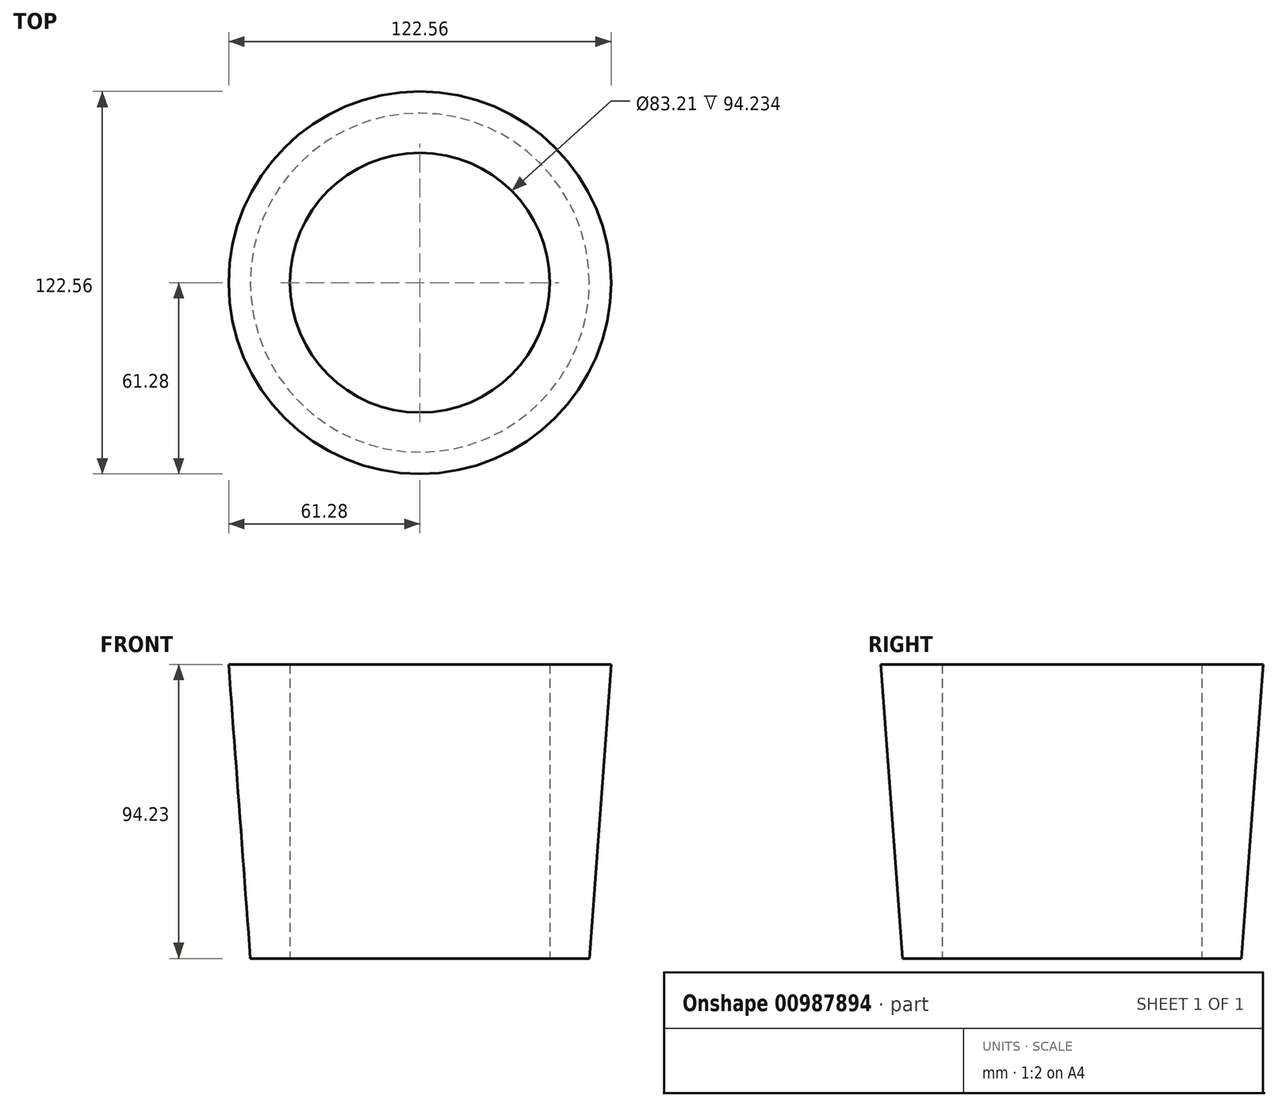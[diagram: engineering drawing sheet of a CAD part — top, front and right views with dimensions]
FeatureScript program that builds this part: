
annotation { "Feature Type Name" : "Feature", "Feature Type Description" : "" }
export const myFeature = defineFeature(function(context is Context, id is Id, definition is map)
    precondition{}
    {
        {
            var Q0;
            Q0=qCreatedBy(makeId("Front.planeOp"),FACE);
            var sketch = newSketch(context, id + "F0", { "sketchPlane" : qUnion([Q0])});
            skLineSegment(sketch, "E0", {"start": v(0, 0) * mm, "end": v(0, 44.65) * mm, "construction": true});
            skLineSegment(sketch, "E1", {"start": v(-61.28, 51.18) * mm, "end": v(-54.3, -43.05) * mm});
            skLineSegment(sketch, "E2", {"start": v(-54.3, -43.05) * mm, "end": v(-41.6, -43.05) * mm});
            skLineSegment(sketch, "E3", {"start": v(-54.3, -43.05) * mm, "end": v(0, -43.05) * mm, "construction": true});
            skLineSegment(sketch, "E4", {"start": v(-41.6, -43.05) * mm, "end": v(-41.6, 51.18) * mm});
            skLineSegment(sketch, "E5", {"start": v(-61.28, 51.18) * mm, "end": v(-41.6, 51.18) * mm});
            skLineSegment(sketch, "E6", {"start": v(-41.6, 51.18) * mm, "end": v(-36.53, 51.18) * mm});
            skLineSegment(sketch, "E7", {"start": v(-41.6, -43.05) * mm, "end": v(-36.53, 51.18) * mm});
            skSolve(sketch);
        }
        {
            var Q0;
            Q0=makeQuery(id+"F0.imprint","IMPRINT",FACE,{"disambiguationData":[TD([[makeQuery(id+"F0.imprint","IMPRINT",EDGE,{"derivedFrom":sQuery(id+"F0.wireOp",EDGE,"E1")}),1.0]])]});
            var Q1;
            Q1=sQuery(id+"F0.wireOp",EDGE,"E0");
            revolve(context, id + "F1", {"surfaceOperationType" : NewSurfaceOperationType.NEW, "entities" : qUnion([Q0]), "axis" : qUnion([Q1]), "revolveType" : RevolveType.FULL});
        }
    });
